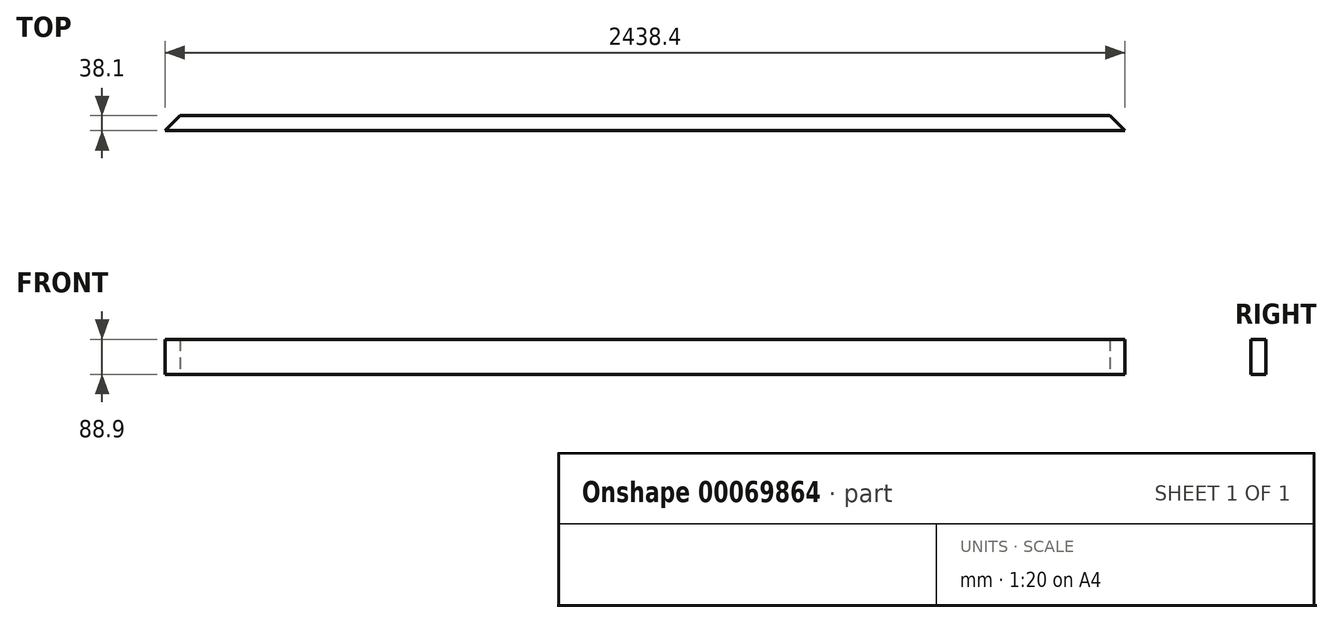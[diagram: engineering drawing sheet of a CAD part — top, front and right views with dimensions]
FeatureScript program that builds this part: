
annotation { "Feature Type Name" : "Feature", "Feature Type Description" : "" }
export const myFeature = defineFeature(function(context is Context, id is Id, definition is map)
    precondition{}
    {
        {
            var Q0;
            Q0=qCreatedBy(makeId("Top.planeOp"),FACE);
            var sketch = newSketch(context, id + "F1", { "sketchPlane" : qUnion([Q0])});
            skLineSegment(sketch, "E0.rect.bottom", {"start": v(1181.1, 19.05) * mm, "end": v(-1181.1, 19.05) * mm});
            skLineSegment(sketch, "E0.rect.top", {"start": v(1219.2, -19.05) * mm, "end": v(-1219.2, -19.05) * mm});
            skPoint(sketch, "E0.rect.middle", {"position": v(0, 0) * mm});
            skLineSegment(sketch, "E1", {"start": v(1219.2, -19.05) * mm, "end": v(1181.1, 19.05) * mm});
            skLineSegment(sketch, "E2", {"start": v(-1219.2, -19.05) * mm, "end": v(-1181.1, 19.05) * mm});
            skPoint(sketch, "E0.rect.left.start.orphan", {"position": v(1219.2, 19.05) * mm});
            skPoint(sketch, "E0.rect.right.start.orphan", {"position": v(-1219.2, 19.05) * mm});
            skSolve(sketch);
        }
        {
            var Q0;
            Q0=makeQuery(id+"F1.imprint","IMPRINT",FACE,{"disambiguationData":[TD([[makeQuery(id+"F1.imprint","IMPRINT",EDGE,{"derivedFrom":sQuery(id+"F1.wireOp",EDGE,"E0.rect.bottom")}),1.0]])]});
            extrude(context, id + "F0", {"entities" : qUnion([Q0]), "depth" : 88.9 * mm});
        }
    });
